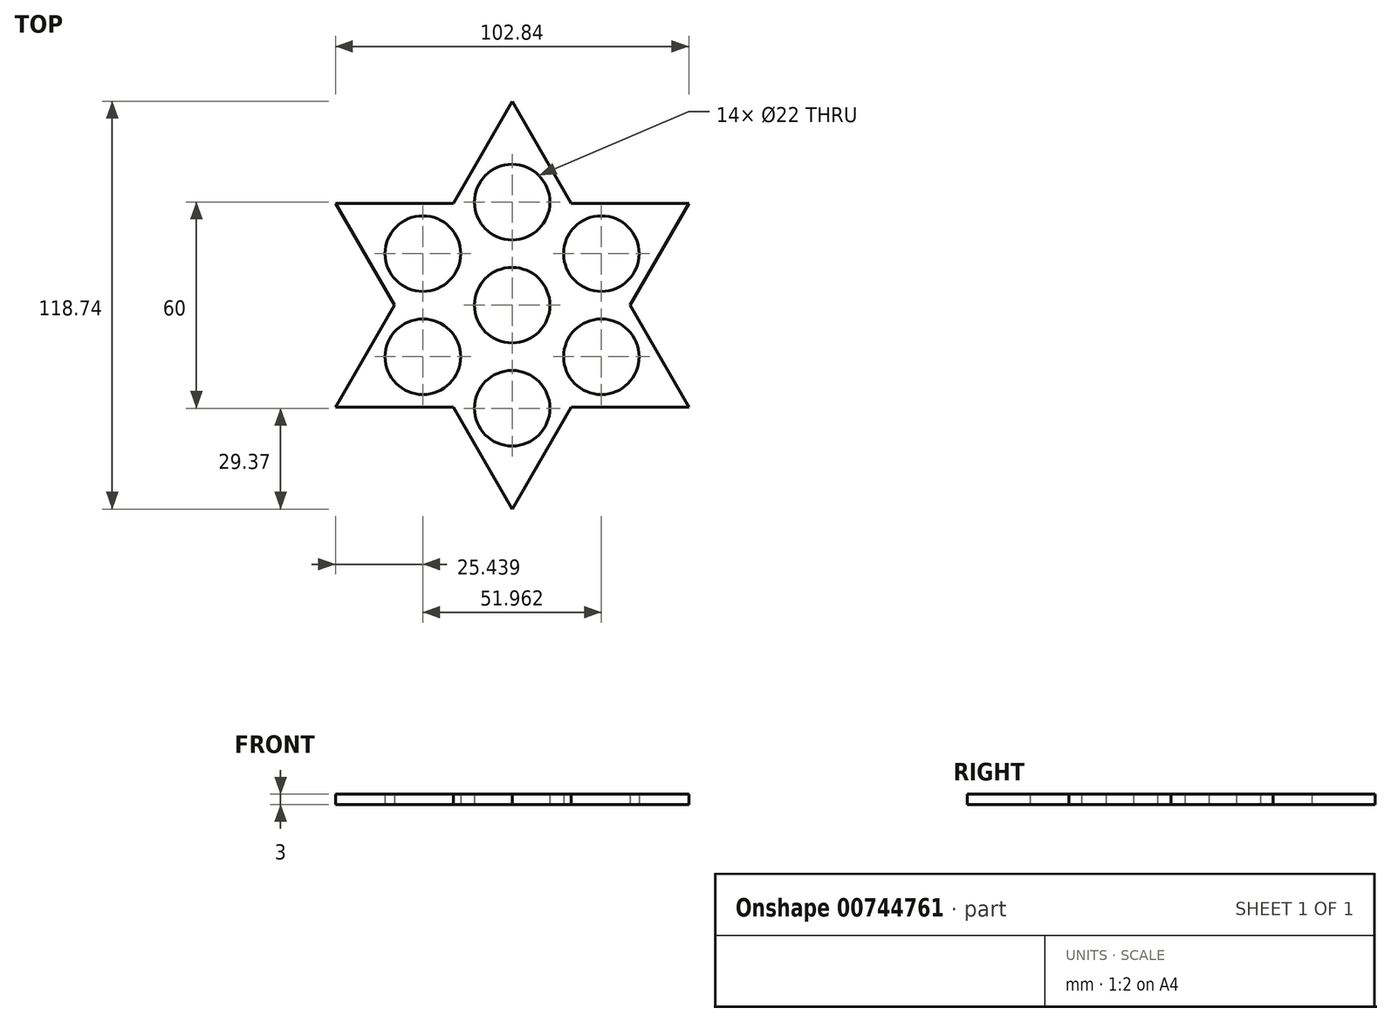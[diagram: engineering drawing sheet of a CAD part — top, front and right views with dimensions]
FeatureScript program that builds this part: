
annotation { "Feature Type Name" : "Feature", "Feature Type Description" : "" }
export const myFeature = defineFeature(function(context is Context, id is Id, definition is map)
    precondition{}
    {
        {
            var Q0;
            Q0=qCreatedBy(makeId("Top.planeOp"),FACE);
            var sketch = newSketch(context, id + "F0", { "sketchPlane" : qUnion([Q0])});
            skCircle(sketch, "E0", {"center": v(0, 0) * mm, "radius": 11 * mm});
            skPoint(sketch, "E1.start.orphan", {"position": v(0, -64.33) * mm});
            skLineSegment(sketch, "E2", {"start": v(0, 11) * mm, "end": v(0, 19) * mm});
            skCircle(sketch, "E3", {"center": v(0, 30) * mm, "radius": 11 * mm});
            skCircle(sketch, "E4", {"center": v(25.98, 15) * mm, "radius": 11 * mm});
            skCircle(sketch, "E5", {"center": v(25.98, -15) * mm, "radius": 11 * mm});
            skCircle(sketch, "E6", {"center": v(0, -30) * mm, "radius": 11 * mm});
            skCircle(sketch, "E7", {"center": v(-25.98, -15) * mm, "radius": 11 * mm});
            skCircle(sketch, "E8", {"center": v(-25.98, 15) * mm, "radius": 11 * mm});
            skLineSegment(sketch, "E9.3", {"start": v(50.87, 30) * mm, "end": v(51.42, 29.69) * mm});
            skArc(sketch, "E10.trimOffspring", {"start": v(51.42, 29.69) * mm, "mid": v(51.33, 29.84) * mm, "end": v(51.24, 30) * mm, "construction": true});
            skLineSegment(sketch, "E11.trimOffspring", {"start": v(50.87, 30) * mm, "end": v(51.24, 30) * mm});
            skLineSegment(sketch, "E12", {"start": v(-51.42, 29.69) * mm, "end": v(-17.14, 29.69) * mm});
            skLineSegment(sketch, "E13", {"start": v(51.42, 29.69) * mm, "end": v(34.28, 0) * mm});
            skLineSegment(sketch, "E14", {"start": v(0, -59.37) * mm, "end": v(-17.14, -29.69) * mm});
            skLineSegment(sketch, "E15", {"start": v(0, 59.37) * mm, "end": v(-17.14, 29.69) * mm});
            skLineSegment(sketch, "E16", {"start": v(-51.42, -29.69) * mm, "end": v(-17.14, -29.69) * mm});
            skLineSegment(sketch, "E17", {"start": v(0, 59.37) * mm, "end": v(17.14, 29.69) * mm});
            skLineSegment(sketch, "E18.trimOffspring", {"start": v(-25.7, 14.84) * mm, "end": v(-25.98, 15) * mm});
            skLineSegment(sketch, "E19.trimOffspring", {"start": v(17.14, 29.69) * mm, "end": v(51.42, 29.69) * mm});
            skLineSegment(sketch, "E20.trimOffspring", {"start": v(-34.28, 0) * mm, "end": v(-51.42, -29.69) * mm});
            skLineSegment(sketch, "E21.trimOffspring", {"start": v(-34.28, 0) * mm, "end": v(-51.42, 29.69) * mm});
            skLineSegment(sketch, "E22.trimOffspring", {"start": v(-25.7, -14.84) * mm, "end": v(-25.98, -15) * mm});
            skLineSegment(sketch, "E23.trimOffspring", {"start": v(17.14, -29.69) * mm, "end": v(51.42, -29.69) * mm});
            skLineSegment(sketch, "E24.trimOffspring", {"start": v(0, -29.69) * mm, "end": v(0, -30) * mm});
            skLineSegment(sketch, "E25.trimOffspring", {"start": v(17.14, -29.69) * mm, "end": v(0, -59.37) * mm});
            skLineSegment(sketch, "E26.trimOffspring", {"start": v(34.28, 0) * mm, "end": v(51.42, -29.69) * mm});
            skSolve(sketch);
        }
        {
            var Q0;
            Q0=makeQuery(id+"F0.imprint","IMPRINT",FACE,{"disambiguationData":[TD([[makeQuery(id+"F0.imprint","IMPRINT",EDGE,{"derivedFrom":sQuery(id+"F0.wireOp",EDGE,"E0")}),-1.0]])]});
            extrude(context, id + "F1", {"entities" : qUnion([Q0]), "depth" : 3 * mm, "offsetDistance" : 25 * mm});
        }
    });
